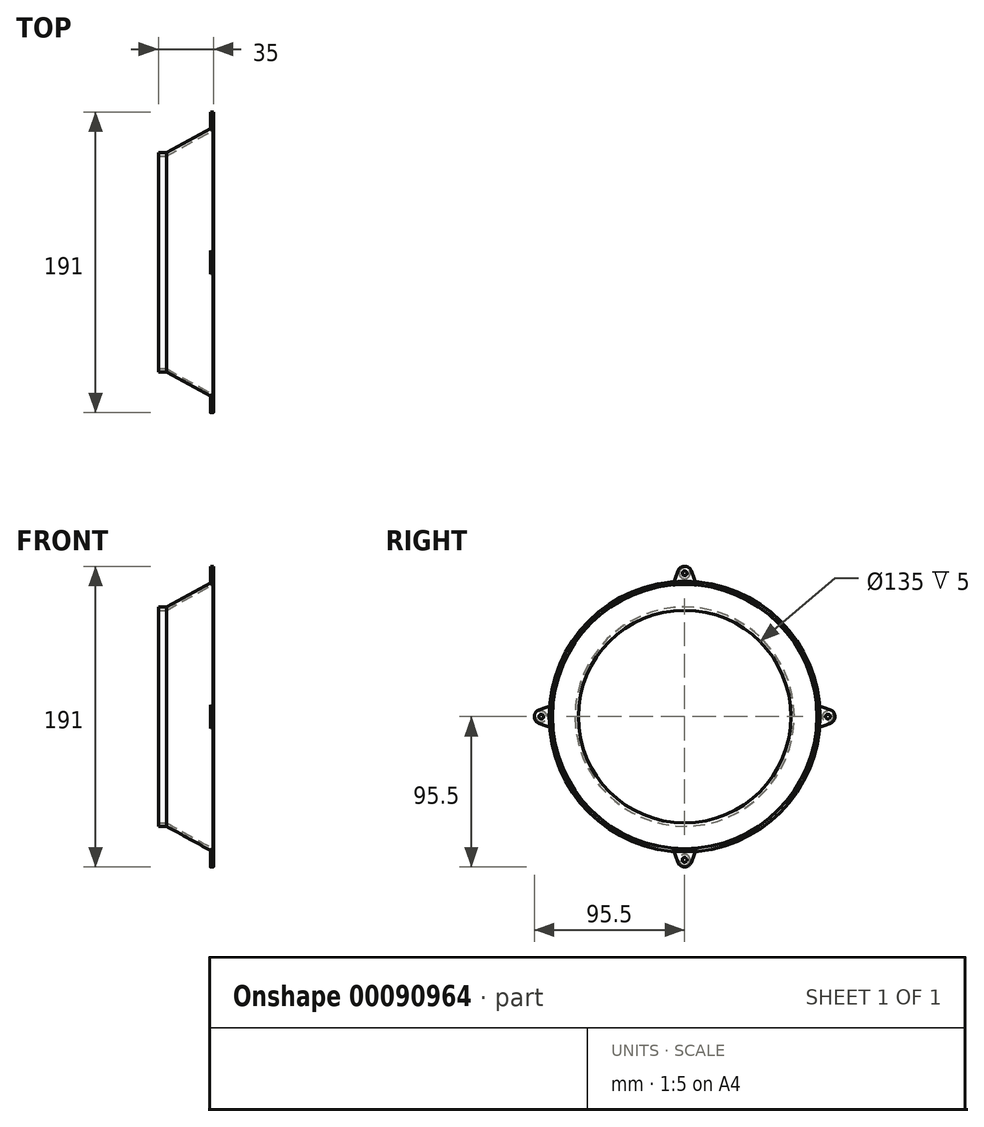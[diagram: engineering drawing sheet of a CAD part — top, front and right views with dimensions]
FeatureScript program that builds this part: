
annotation { "Feature Type Name" : "Feature", "Feature Type Description" : "" }
export const myFeature = defineFeature(function(context is Context, id is Id, definition is map)
    precondition{}
    {
        {
            var Q0;
            Q0=qCreatedBy(makeId("Top.planeOp"),FACE);
            var sketch = newSketch(context, id + "F0", { "sketchPlane" : qUnion([Q0])});
            skLineSegment(sketch, "E0", {"start": v(-30, 67.5) * mm, "end": v(-35, 67.5) * mm});
            skLineSegment(sketch, "E1", {"start": v(-35, 67.5) * mm, "end": v(-35, 69.6) * mm});
            skLineSegment(sketch, "E2", {"start": v(-35, 69.6) * mm, "end": v(-30, 69.6) * mm});
            skLineSegment(sketch, "E3", {"start": v(-30, 69.6) * mm, "end": v(-0.18, 86) * mm});
            skLineSegment(sketch, "E4", {"start": v(0, 0) * mm, "end": v(-52.35, 0) * mm, "construction": true});
            skLineSegment(sketch, "E5", {"start": v(-15.1, 77.8) * mm, "end": v(-15.1, 75.7) * mm, "construction": true});
            skLineSegment(sketch, "E6", {"start": v(0, 86) * mm, "end": v(0, 84) * mm});
            skLineSegment(sketch, "E7", {"start": v(0, 84) * mm, "end": v(-30, 67.5) * mm});
            skLineSegment(sketch, "E8", {"start": v(-0.18, 86) * mm, "end": v(0, 86) * mm});
            skSolve(sketch);
        }
        {
            var Q0;
            Q0=qSketchRegion(id+"F0",true);
            var Q1;
            Q1=sQuery(id+"F0.wireOp",EDGE,"E4");
            revolve(context, id + "F1", {"entities" : qUnion([Q0]), "axis" : qUnion([Q1]), "revolveType" : RevolveType.FULL});
        }
        {
            var Q0;
            Q0=makeQuery(id+"F1.opRevolve","SWEPT_FACE",FACE,{"disambiguationData":[OSD([sQuery(id+"F0.wireOp",EDGE,"E6")])]});
            var sketch = newSketch(context, id + "F2", { "sketchPlane" : qUnion([Q0])});
            skCircle(sketch, "E9", {"center": v(-91, 0) * mm, "radius": 1.5 * mm});
            skLineSegment(sketch, "E10", {"start": v(0, 0) * mm, "end": v(-58.25, 0) * mm, "construction": true});
            skLineSegment(sketch, "E11", {"start": v(-86, 0) * mm, "end": v(-96, 0) * mm, "construction": true});
            skLineSegment(sketch, "E12", {"start": v(-83.67, -7.46) * mm, "end": v(-92.54, -4.23) * mm});
            skLineSegment(sketch, "E13", {"start": v(-83.67, 7.46) * mm, "end": v(-92.54, 4.23) * mm});
            skArc(sketch, "E14", {"start": v(-92.54, 4.23) * mm, "mid": v(-95.5, 0) * mm, "end": v(-92.54, -4.23) * mm});
            skArc(sketch, "E15.0", {"start": v(-83.67, 7.46) * mm, "mid": v(-84, 0) * mm, "end": v(-83.67, -7.46) * mm});
            skSolve(sketch);
        }
        {
            var Q0;
            Q0=qSketchRegion(id+"F2",true);
            extrude(context, id + "F3", {"entities" : qUnion([Q0]), "oppositeDirection" : true, "depth" : 2 * mm});
        }
        {
            var Q0;
            Q0=makeQuery(id+"F3.opExtrude","SWEPT_BODY",BODY,{"disambiguationData":[OSD([sQuery(id+"F2.wireOp",EDGE,"E9")])]});
            var Q1;
            Q1=makeQuery(id+"F1.opRevolve","SWEPT_EDGE",EDGE,{"disambiguationData":[OSD([sQuery(id+"F0.wireOp",EDGE,"E0"),sQuery(id+"F0.wireOp",EDGE,"E1")])]});
            circularPattern(context, id + "F4", {"entities" : qUnion([Q0]), "axis" : qUnion([Q1]), "angle" : 90 * degree, "instanceCount" : 4});
        }
        {
            var Q0;
            Q0=makeQuery(id+"FBsMdyETQllmhCt_2.opBoolean","COPY",EDGE,{"derivedFrom":makeQuery(id+"F3.opExtrude","CAP_EDGE",EDGE,{"disambiguationData":[OSD([sQuery(id+"F2.wireOp",EDGE,"E9")])],"isStart":true})});
            var Q1;
            Q1=makeQuery(id+"FBsMdyETQllmhCt_2.opBoolean","COPY",EDGE,{"derivedFrom":makeQuery(id+"F4.opPattern","COPY",EDGE,{"derivedFrom":makeQuery(id+"F3.opExtrude","CAP_EDGE",EDGE,{"disambiguationData":[OSD([sQuery(id+"F2.wireOp",EDGE,"E9")])],"isStart":true}),"instanceName":"3"})});
            var Q2;
            Q2=makeQuery(id+"FBsMdyETQllmhCt_2.opBoolean","COPY",EDGE,{"derivedFrom":makeQuery(id+"F4.opPattern","COPY",EDGE,{"derivedFrom":makeQuery(id+"F3.opExtrude","CAP_EDGE",EDGE,{"disambiguationData":[OSD([sQuery(id+"F2.wireOp",EDGE,"E9")])],"isStart":true}),"instanceName":"2"})});
            var Q3;
            Q3=makeQuery(id+"FBsMdyETQllmhCt_2.opBoolean","COPY",EDGE,{"derivedFrom":makeQuery(id+"F4.opPattern","COPY",EDGE,{"derivedFrom":makeQuery(id+"F3.opExtrude","CAP_EDGE",EDGE,{"disambiguationData":[OSD([sQuery(id+"F2.wireOp",EDGE,"E9")])],"isStart":true}),"instanceName":"1"})});
            var Q4;
            Q4=makeQuery(id+"F3.opExtrude","CAP_EDGE",EDGE,{"disambiguationData":[OSD([sQuery(id+"F2.wireOp",EDGE,"E9")])],"isStart":false});
            var Q5;
            Q5=makeQuery(id+"F4.opPattern","COPY",EDGE,{"derivedFrom":makeQuery(id+"F3.opExtrude","CAP_EDGE",EDGE,{"disambiguationData":[OSD([sQuery(id+"F2.wireOp",EDGE,"E9")])],"isStart":false}),"instanceName":"3"});
            var Q6;
            Q6=makeQuery(id+"F4.opPattern","COPY",EDGE,{"derivedFrom":makeQuery(id+"F3.opExtrude","CAP_EDGE",EDGE,{"disambiguationData":[OSD([sQuery(id+"F2.wireOp",EDGE,"E9")])],"isStart":false}),"instanceName":"2"});
            var Q7;
            Q7=makeQuery(id+"F4.opPattern","COPY",EDGE,{"derivedFrom":makeQuery(id+"F3.opExtrude","CAP_EDGE",EDGE,{"disambiguationData":[OSD([sQuery(id+"F2.wireOp",EDGE,"E9")])],"isStart":false}),"instanceName":"1"});
            chamfer(context, id + "F5", {"entities" : qUnion([Q0, Q1, Q2, Q3, Q4, Q5, Q6, Q7]), "width" : 2 * mm, "tangentPropagation" : true});
        }
    });
